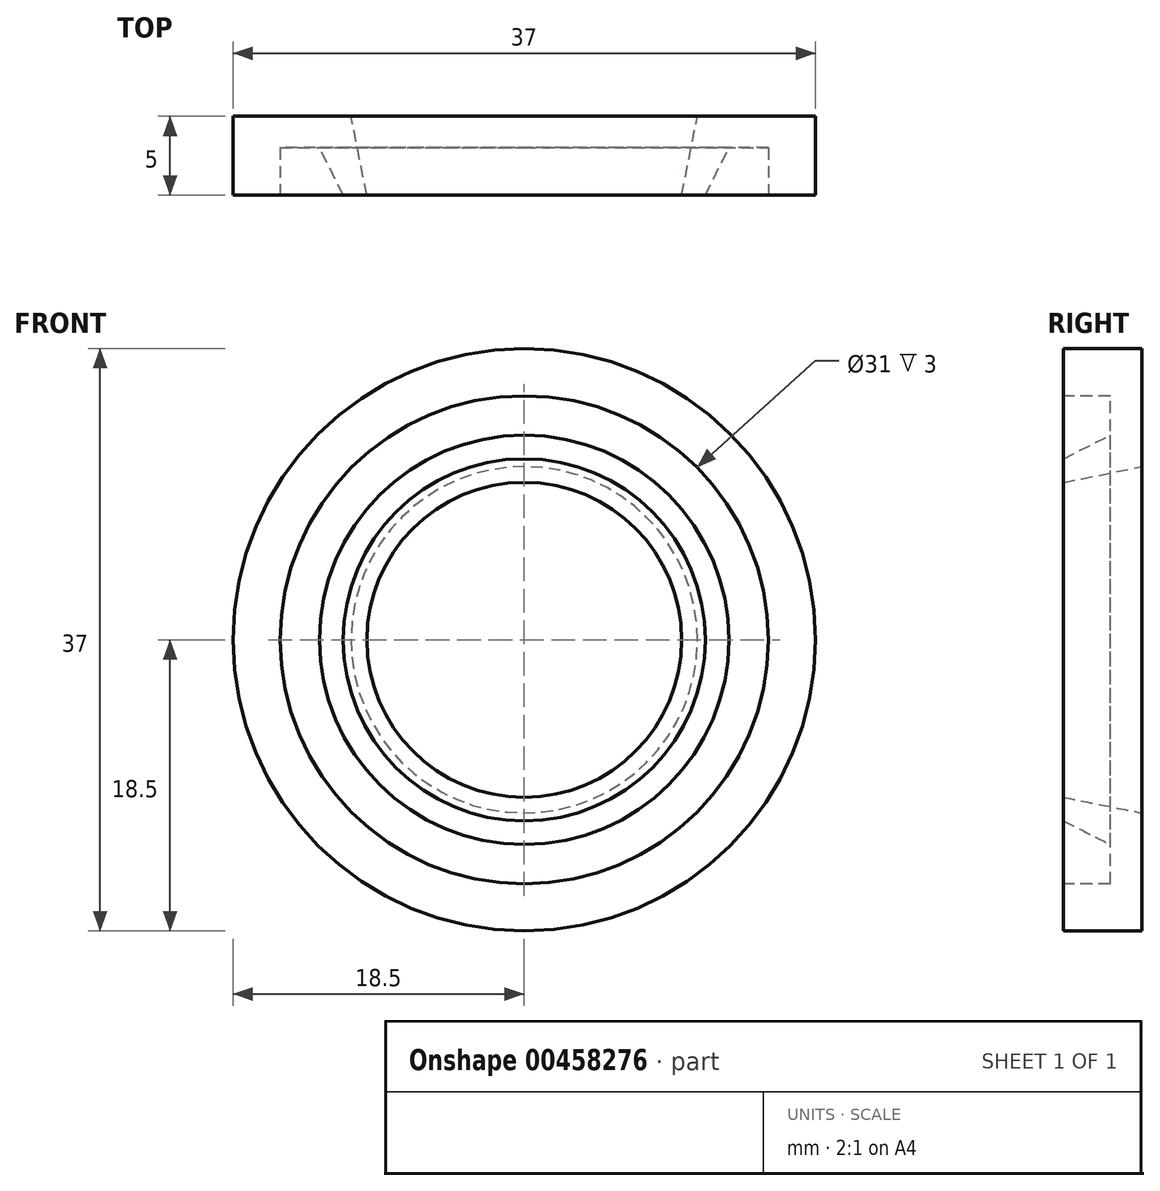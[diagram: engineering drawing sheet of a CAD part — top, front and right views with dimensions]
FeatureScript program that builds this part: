
annotation { "Feature Type Name" : "Feature", "Feature Type Description" : "" }
export const myFeature = defineFeature(function(context is Context, id is Id, definition is map)
    precondition{}
    {
        {
            var Q0;
            Q0=qCreatedBy(makeId("Right.planeOp"),FACE);
            var sketch = newSketch(context, id + "F0", { "sketchPlane" : qUnion([Q0])});
            skLineSegment(sketch, "E0", {"start": v(0, 0) * mm, "end": v(-5, 0) * mm, "construction": true});
            skLineSegment(sketch, "E1", {"start": v(-5, 0) * mm, "end": v(-5, 10) * mm, "construction": true});
            skLineSegment(sketch, "E2", {"start": v(-5, 10) * mm, "end": v(-5, 11.5) * mm});
            skLineSegment(sketch, "E3", {"start": v(0, 0) * mm, "end": v(0, 11) * mm, "construction": true});
            skLineSegment(sketch, "E4", {"start": v(0, 11) * mm, "end": v(-5, 10) * mm});
            skLineSegment(sketch, "E5", {"start": v(0, 0) * mm, "end": v(-2, 0) * mm, "construction": true});
            skLineSegment(sketch, "E6", {"start": v(-2, 0) * mm, "end": v(-2, 13) * mm, "construction": true});
            skLineSegment(sketch, "E7", {"start": v(-5, 11.5) * mm, "end": v(-2, 13) * mm});
            skLineSegment(sketch, "E8", {"start": v(0, 11) * mm, "end": v(0, 18.5) * mm});
            skLineSegment(sketch, "E9", {"start": v(0, 18.5) * mm, "end": v(-5, 18.5) * mm});
            skLineSegment(sketch, "E10", {"start": v(-5, 18.5) * mm, "end": v(-5, 15.5) * mm});
            skLineSegment(sketch, "E11", {"start": v(-5, 15.5) * mm, "end": v(-2, 15.5) * mm});
            skLineSegment(sketch, "E12", {"start": v(-2, 15.5) * mm, "end": v(-2, 13) * mm});
            skLineSegment(sketch, "E13", {"start": v(-10.46, 0) * mm, "end": v(12.18, 0) * mm});
            skSolve(sketch);
        }
        {
            var Q0;
            Q0=makeQuery(id+"F0.imprint","IMPRINT",FACE,{"disambiguationData":[TD([[makeQuery(id+"F0.imprint","IMPRINT",EDGE,{"derivedFrom":sQuery(id+"F0.wireOp",EDGE,"E2")}),-1.0]])]});
            var Q1;
            Q1=sQuery(id+"F0.wireOp",EDGE,"E13");
            revolve(context, id + "F1", {"entities" : qUnion([Q0]), "axis" : qUnion([Q1]), "revolveType" : RevolveType.FULL});
        }
    });
